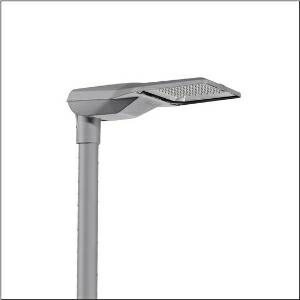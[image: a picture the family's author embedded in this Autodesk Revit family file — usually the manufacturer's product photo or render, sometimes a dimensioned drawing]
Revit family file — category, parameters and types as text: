
# Revit family: streetlight_sl_21_iq_midi___stw1_0a_5xe3e41d08mb_aeb4
name_source: partatom
category: Lighting Fixtures
units: mm (PartAtom-declared; Revit-internal decimal feet)

## family parameters
Cut with Voids When Loaded = No
Host = Face
Light Source = No
Part Type = Normal
Room Calculation Point = No
Round Connector Dimension = Use Diameter
Shared = No

## types (1)
- --- (1 x LED, 20360 lm, 146.7 W, 4000K)
    Apparent Load = 147 VA
    CIE Flux Codes = 38 75 98 100 100
    Color Rendering = 70
    Color Temperature = 4000K
    Default Elevation = 1800 mm
    Description = Streetlight SL 21 iQ midi, mast luminaire, primary light control with lens, of PMMA, primary optical cover: cover, of toughened safety glass, transparent, light distribution: STW1.0a, light emission: direct distribution, primary light characteristic: asymmetric, installation type: post-top, side-entry, LED, High Power LED, rated luminous flux: 20.360lm, luminous efficacy: 139lm/W, light colour: 740, colour temperature: 4000K, control gear: iQ-Comfort, control: Auto-Match, Temp-Guard, Lumen-Switch, Night-Set, Smart-Wire, Light-Fading, Desk-Remote (wireless, voltage-free reading and setting of iQ features in the workshop via application-optimized NFC function/RFID function), optimised constant luminous flux control (CLO 2.0), pre-setting: linear dimming characteristic, mains connection: 230..240V, AC, 50/60Hz, start of lifetime: 147W, end of service life: 161W, reduction: 62W, luminaire housing, of diecast aluminium, powder-coated, SITECO metallic grey (DB 702S), corrosivity category C5 high according to DIN EN ISO 12944, please order mast flange separately, inclination adjustable: 0°, 5°, 10°, 15°, sealing non-destructively replaceable, multi-level sealing system, length: 644mm, width: 335mm, height: 110mm, mast flange for spigot size: 42mm (side-entry): 5XC10008XM4, 60/48mm (side-entry/post-top): 5XC10108XM2, 76/60mm (side-entry/post-top): 5XC10108XM1, mounting height: 4..8m, protection rating (complete): IP66, insulation class (complete): insulation class II (safety insulation), certification: CE, ENEC, ENEC+, VDE, impact resistance: IK10, permissible operating ambient temperature for outdoor applications: -40..+50°C, standard-compliant lighting for roads and squares, packaging unit: 1 piece

Light Distribution: STW1.0a
    Height = 111 mm
    Lamp = 1 x LED
    Lamp Light Flux = 20360 lm
    Lamp Power = 146.7 W
    Lamp count = 1
    Length = 644 mm
    Luminous efficacy = 139 lm/W
    Manufacturer = Siteco
    ModVariant = No
    Model = 5XE3E41D08MB
    Number of Poles = 1
    OnlyDefault = Yes
    Power Factor = 1
    Product Name = Streetlight SL 21 iQ midi | STW1.0a
    Product group = mast luminaire | pylon top
    ProductGroupID = 6100
    Protection Class = Protection class II
    Protection Degree = IP 66
    RLX_Detail_Level = 1
    RLX_Emergency_Light_Flux = 0 lm
    RLX_Emergency_Type = 0
    RLX_Emergency_Type_DB = No
    RlxData = <blob elided: 26965 chars, md5=107ae427>
    Socket = socket
    Standby Power = 0 W
    System Light Flux = 20360 lm
    System Power = 147 W
    Type Comments = factory setting: luminous flux: 100 % | dim-lin: 254 | 753 mA
    Type Image = l_1004298.jpg
    URL = http://relux.com
    VarID = @adj_185525
    Voltage = 0 V
    Weight = 0.00 kg
    Width = 336 mm

## geometry (parser evidence)
native form markers: Blend x4, Sweep x13
no freeform markers — native parametric forms only
